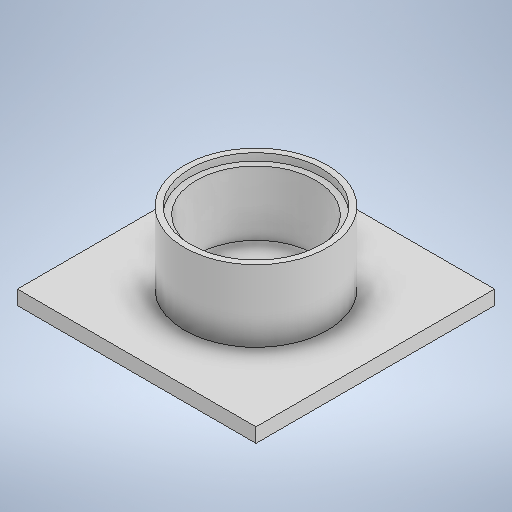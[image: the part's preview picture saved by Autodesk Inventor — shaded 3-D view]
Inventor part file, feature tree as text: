
AUTODESK INVENTOR PART (.ipt)
format: ipt  version: 2025.1 (Build 291241020, 241B)  size: 260,096 bytes
history: native  units: in
note: dims shown in document units (in); Inventor stores cm internally (conversion verified against a paired STEP export)
features: extrude x3, sketch x3
ambient origin geometry x8: Origin, YZ Plane, XZ Plane, XY Plane, X Axis, Y Axis, Z Axis, Center Point
bodies: Solid1 (feature_tree)
feature tree (6):
  extrude  "Extrusion1"  Depth=29.9367in
  extrude  "Extrusion2"  Depth=15.0in
  extrude  "Extrusion3"  Depth=1.5in
  sketch  "Sketch1"  dims[d0=25.0in d1=29.9367in]
  sketch  "Sketch2"  dims[d2=15.0in d3=0.0in d4=25.0in]
  sketch  "Sketch3"  dims[d5=25.0in d6=25.0in d7=25.0in d8=3.0in d9=0.0in d10=1.2in d11=29.9367in d12=1.2683in d13=1.5in d14=0.0in d15=0.5in d16=0.0344in]
